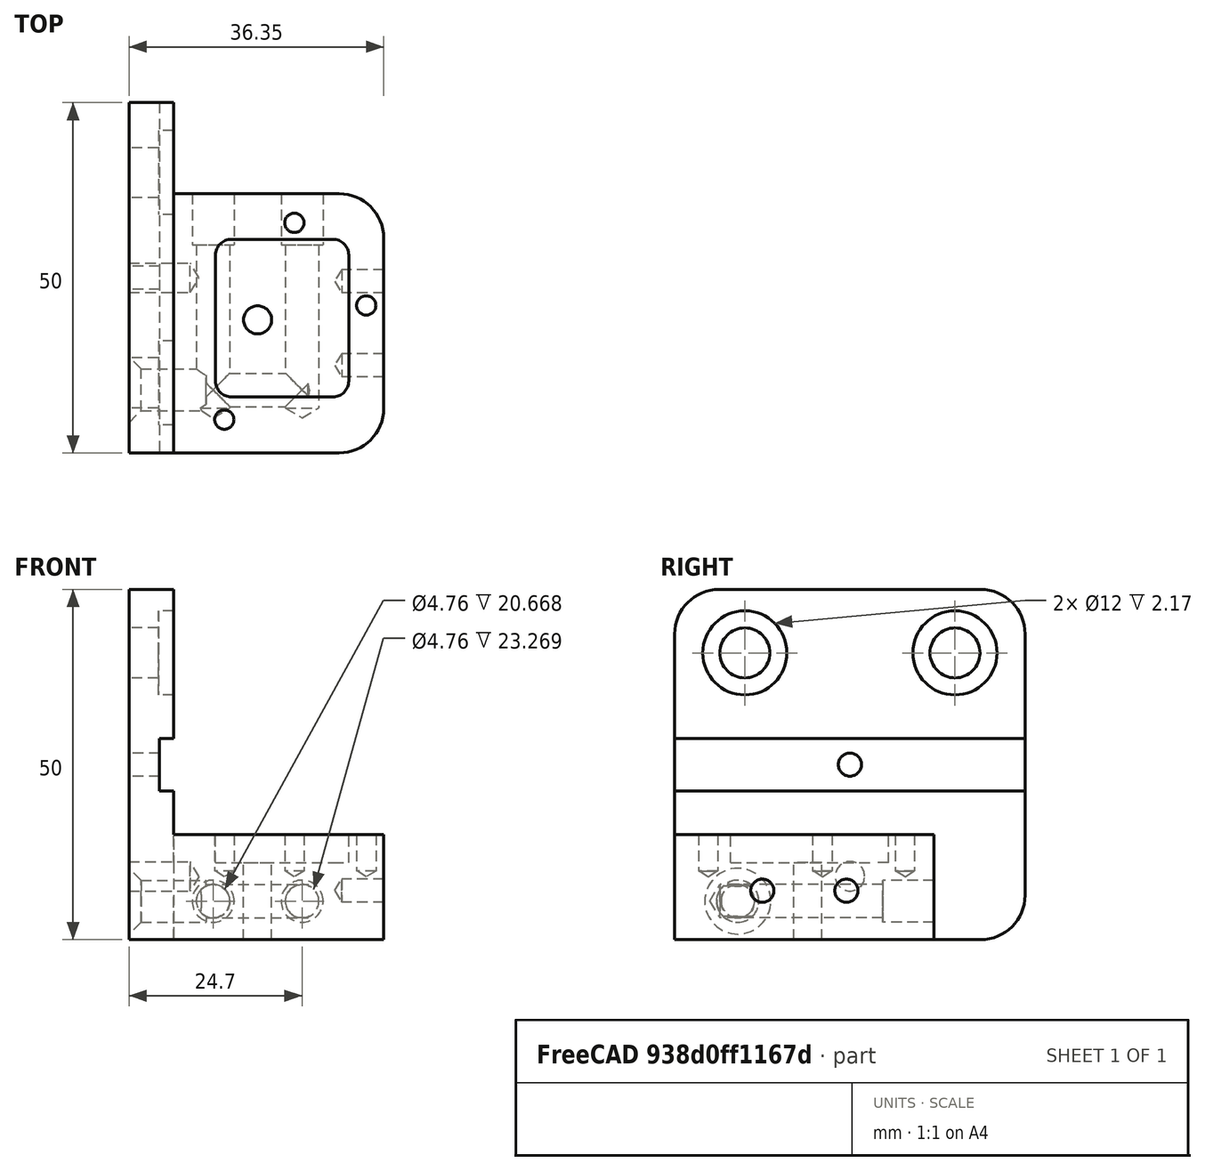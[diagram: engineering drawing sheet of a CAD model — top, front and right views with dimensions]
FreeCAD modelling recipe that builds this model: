
FCSTD DOCUMENT  (FreeCAD 0.19R24267 (Git))
Label: watercooled_block
License: All rights reserved
LicenseURL: http://en.wikipedia.org/wiki/All_rights_reserved
objects: TechDraw::DrawViewDimension×38, Sketcher::SketchObject×11, PartDesign::CoordinateSystem×10, TechDraw::DrawViewAnnotation×9, TechDraw::DrawLeaderLine×9, PartDesign::Hole×8, TechDraw::DrawProjGroupItem×6, PartDesign::Pad×2, PartDesign::Pocket×1, PartDesign::Fillet×1, PartDesign::Chamfer×1, PartDesign::Body×1, TechDraw::DrawSVGTemplate×1, TechDraw::DrawViewPart×1, TechDraw::DrawProjGroup×1, TechDraw::DrawPage×1, App::Part×1
note: 48 computed .brp shape members not serialized (recipe doc carries the construction recipe); baked Part::Feature solids carry a one-line shape summary decoded from their .brp

FEATURE [Sketcher::SketchObject] Sketch051
  FullyConstrained = false
  MapMode = 5
  Placement = pos=(0,0,0) rot=(1,0,0;1.5708rad)
  Support = -> [XZ_Plane061]
  sketch-geometry (10):
    g0: LineSegment StartX=18 StartY=0 StartZ=0 EndX=18 EndY=11 EndZ=0
    g1: LineSegment StartX=18 StartY=11 StartZ=0 EndX=-12 EndY=11 EndZ=0
    g2: LineSegment StartX=-18.35 StartY=0 StartZ=0 EndX=-18.35 EndY=50 EndZ=0
    g3: LineSegment StartX=-18.35 StartY=50 StartZ=0 EndX=-12 EndY=50 EndZ=0
    g4: LineSegment StartX=-12 StartY=50 StartZ=0 EndX=-12 EndY=28.75 EndZ=0
    g5: LineSegment StartX=-18.35 StartY=0 StartZ=0 EndX=18 EndY=0 EndZ=0
    g6: LineSegment StartX=-12 StartY=28.75 StartZ=0 EndX=-14 EndY=28.75 EndZ=0
    g7: LineSegment StartX=-14 StartY=28.75 StartZ=0 EndX=-14 EndY=21.25 EndZ=0
    g8: LineSegment StartX=-14 StartY=21.25 StartZ=0 EndX=-12 EndY=21.25 EndZ=0
    g9: LineSegment StartX=-12 StartY=21.25 StartZ=0 EndX=-12 EndY=11 EndZ=0
  constraints (29):
    c: Coincident(g0,g1)
    c: Horizontal(g1)
    c: Vertical(g0)
    c: Coincident(g2,g3)
    c: Coincident(g3,g4)
    c: Horizontal(g3)
    c: Vertical(g2)
    c: Vertical(g4)
    c: DistanceX(g3,g3) = 6.35
    c: DistanceX(g1,g-1) = 12
    c: Coincident(g1,g9)
    c: DistanceY(g0,g0) = 11
    c: DistanceY(g2,g2) = 50
    c: DistanceX(g-1,g0) = 18
    c: Coincident(g5,g2)
    c: Coincident(g5,g0)
    c: Horizontal(g5)
    c: PointOnObject(g-1,g5)
    c: Horizontal(g6)
    c: Coincident(g7,g6)
    c: Vertical(g7)
    c: Coincident(g8,g7)
    c: Horizontal(g8)
    c: Coincident(g4,g6)
    c: Coincident(g9,g8)
    c: Tangent(g4,g9)
    c: DistanceY(g7,g7) = 7.5
    c: DistanceY(g-1,g8) = 21.25
    c: DistanceX(g6,g6) = 2
FEATURE [PartDesign::Pad] Pad021  label="Pad022"
  AllowMultiFace = false
  Direction = (1,1,1)
  Length = 50
  Length2 = 100
  Midplane = true
  Placement = pos=(0,0,0) rot=(1,0,0;1.5708rad)
  Profile = -> Sketch051
  Type = 0
FEATURE [Sketcher::SketchObject] Sketch052
  AttachmentOffset = pos=(0,0,12) rot=(0,0,1;0rad)
  FullyConstrained = false
  MapMode = 5
  Placement = pos=(0,12,2.7e-15) rot=(0,0.707107,0.707107;3.14159rad)
  Support = -> [XZ_Plane061]
  sketch-geometry (3):
    g0: Circle CenterX=-6.35 CenterY=5.5 CenterZ=0 NormalX=0 NormalY=0 NormalZ=1 AngleXU=0 Radius=3.175
    g1: Circle CenterX=6.35 CenterY=5.5 CenterZ=0 NormalX=0 NormalY=0 NormalZ=1 AngleXU=0 Radius=3.175
    g2: LineSegment StartX=-6.35 StartY=5.5 StartZ=0 EndX=6.35 EndY=5.5 EndZ=0
  constraints (8):
    c: Diameter(g0) = 6.35
    c: Diameter(g1) = 6.35
    c: DistanceY(g-1,g0) = 5.5
    c: Coincident(g2,g0)
    c: Coincident(g2,g1)
    c: Horizontal(g2)
    c: DistanceX(g2,g2) = 12.7
    c: DistanceX(g0,g-1) = 6.35
FEATURE [Sketcher::SketchObject] Sketch053
  AttachmentOffset = pos=(0,0,18.35) rot=(0,0,1;0rad)
  FullyConstrained = false
  MapMode = 5
  Placement = pos=(-18.35,4.1e-15,-4.1e-15) rot=(-0.57735,0.57735,0.57735;4.18879rad)
  Support = -> [YZ_Plane061]
  sketch-geometry (1):
    g0: Circle CenterX=16 CenterY=5.5 CenterZ=0 NormalX=0 NormalY=0 NormalZ=1 AngleXU=0 Radius=2.5
  constraints (3):
    c: Diameter(g0) = 5
    c: DistanceY(g-1,g0) = 5.5
    c: DistanceX(g-1,g0) = 16
FEATURE [PartDesign::Hole] Hole006
  AllowMultiFace = false
  BaseFeature = -> Pad021
  Depth = 27
  DepthType = 0
  Diameter = 4.763
  DrillForDepth = false
  DrillPoint = 1
  DrillPointAngle = 118
  HoleCutCountersinkAngle = 90
  HoleCutCustomValues = false
  HoleCutDepth = 11
  HoleCutDiameter = 6
  HoleCutType = 1
  ModelActualThread = false
  Placement = pos=(0,0,0) rot=(1,0,0;1.5708rad)
  Profile = -> Sketch053
  Tapered = false
  TaperedAngle = 90
  ThreadAngle = 0
  ThreadClass = 0
  ThreadCutOffInner = 0
  ThreadCutOffOuter = 0
  ThreadDirection = 0
  ThreadFit = 0
  ThreadPitch = 0
  ThreadSize = 0
  ThreadType = 0
  Threaded = false
FEATURE [Sketcher::SketchObject] Sketch054
  FullyConstrained = false
  MapMode = 5
  Placement = pos=(0,0,0) rot=(0,1,0;3.14159rad)
  Support = -> [XY_Plane061]
  sketch-geometry (1):
    g0: Circle CenterX=0 CenterY=-6 CenterZ=0 NormalX=0 NormalY=0 NormalZ=1 AngleXU=0 Radius=2
  constraints (3):
    c: Diameter(g0) = 4
    c: PointOnObject(g0,g-2)
    c: DistanceY(g0,g-1) = 6
FEATURE [PartDesign::Hole] Hole007
  AllowMultiFace = false
  BaseFeature = -> Hole006
  Depth = 25
  DepthType = 1
  Diameter = 4
  DrillForDepth = false
  DrillPoint = 1
  DrillPointAngle = 118
  HoleCutCountersinkAngle = 90
  HoleCutCustomValues = false
  HoleCutDepth = 0
  HoleCutDiameter = 0
  HoleCutType = 0
  ModelActualThread = false
  Placement = pos=(0,0,0) rot=(1,0,0;1.5708rad)
  Profile = -> Sketch054
  Tapered = false
  TaperedAngle = 90
  ThreadAngle = 0
  ThreadClass = 0
  ThreadCutOffInner = 0
  ThreadCutOffOuter = 0
  ThreadDirection = 0
  ThreadFit = 0
  ThreadPitch = 0
  ThreadSize = 0
  ThreadType = 0
  Threaded = false
FEATURE [Sketcher::SketchObject] Sketch055
  AttachmentOffset = pos=(0,0,-12) rot=(0,0,1;0rad)
  FullyConstrained = false
  MapMode = 5
  Placement = pos=(-12,2.7e-15,-2.7e-15) rot=(0.57735,0.57735,0.57735;2.0944rad)
  Support = -> [YZ_Plane061]
  expr: Constraints[3] = 25 + 31.9 / 2
  sketch-geometry (2):
    g0: Circle CenterX=-15 CenterY=40.95 CenterZ=0 NormalX=0 NormalY=0 NormalZ=1 AngleXU=0 Radius=2.55
    g1: Circle CenterX=15 CenterY=40.95 CenterZ=0 NormalX=0 NormalY=0 NormalZ=1 AngleXU=0 Radius=2.55
  constraints (5):
    c: Diameter(g1) = 5.1
    c: Equal(g1,g0)
    c: DistanceX(g0,g1) = 30
    c: DistanceY(g-1,g0) = 40.95
    c: Symmetric(g0,g1,g-2)
FEATURE [PartDesign::Hole] Hole008
  AllowMultiFace = false
  BaseFeature = -> Hole007
  Depth = 25
  DepthType = 1
  Diameter = 7.14
  DrillForDepth = false
  DrillPoint = 1
  DrillPointAngle = 118
  HoleCutCountersinkAngle = 90
  HoleCutCustomValues = false
  HoleCutDepth = 2.17
  HoleCutDiameter = 12
  HoleCutType = 1
  ModelActualThread = false
  Placement = pos=(0,0,0) rot=(1,0,0;1.5708rad)
  Profile = -> Sketch055
  Tapered = false
  TaperedAngle = 90
  ThreadAngle = 0
  ThreadClass = 0
  ThreadCutOffInner = 0
  ThreadCutOffOuter = 0
  ThreadDirection = 0
  ThreadFit = 0
  ThreadPitch = 0
  ThreadSize = 0
  ThreadType = 0
  Threaded = false
  expr: HoleCutDepth = 6.35 - 4.18
FEATURE [Sketcher::SketchObject] Sketch056
  AttachmentOffset = pos=(0,0,18.35) rot=(0,0,1;0rad)
  FullyConstrained = false
  MapMode = 5
  Placement = pos=(-18.35,4.1e-15,-4.1e-15) rot=(-0.57735,0.57735,0.57735;4.18879rad)
  Support = -> [YZ_Plane061]
  expr: Constraints[2] = 25 - 31.9 / 2
  sketch-geometry (1):
    g0: Circle CenterX=0 CenterY=9.05 CenterZ=0 NormalX=0 NormalY=0 NormalZ=1 AngleXU=0 Radius=2.5
  constraints (3):
    c: PointOnObject(g0,g-2)
    c: Diameter(g0) = 5
    c: DistanceY(g-1,g0) = 9.05
FEATURE [Sketcher::SketchObject] Sketch057
  AttachmentOffset = pos=(0,0,11) rot=(0,0,1;0rad)
  FullyConstrained = false
  MapMode = 5
  Placement = pos=(0,0,11) rot=(0,0,1;0rad)
  Support = -> [XY_Plane061]
  sketch-geometry (4):
    g0: LineSegment StartX=23 StartY=32 StartZ=0 EndX=-12 EndY=32 EndZ=0
    g1: LineSegment StartX=-12 StartY=32 StartZ=0 EndX=-12 EndY=12 EndZ=0
    g2: LineSegment StartX=-12 StartY=12 StartZ=0 EndX=23 EndY=12 EndZ=0
    g3: LineSegment StartX=23 StartY=12 StartZ=0 EndX=23 EndY=32 EndZ=0
  constraints (12):
    c: Coincident(g0,g1)
    c: Coincident(g1,g2)
    c: Coincident(g2,g3)
    c: Coincident(g3,g0)
    c: Horizontal(g0)
    c: Horizontal(g2)
    c: Vertical(g1)
    c: Vertical(g3)
    c: DistanceX(g1,g-1) = 12
    c: DistanceX(g2,g2) = 35
    c: DistanceY(g3,g3) = 20
    c: DistanceY(g-1,g2) = 12
FEATURE [PartDesign::Pocket] Pocket019
  AllowMultiFace = false
  BaseFeature = -> Hole008
  Length = 5
  Length2 = 100
  Placement = pos=(0,0,0) rot=(1,0,0;1.5708rad)
  Profile = -> Sketch057
  Type = 1
FEATURE [PartDesign::Hole] Hole009
  AllowMultiFace = false
  BaseFeature = -> Pocket019
  Depth = 32
  DepthType = 0
  Diameter = 4.7625
  DrillForDepth = false
  DrillPoint = 1
  DrillPointAngle = 118
  HoleCutCountersinkAngle = 90
  HoleCutCustomValues = false
  HoleCutDepth = 7.3
  HoleCutDiameter = 6
  HoleCutType = 1
  ModelActualThread = false
  Placement = pos=(0,0,0) rot=(1,0,0;1.5708rad)
  Profile = -> Sketch052
  Tapered = false
  TaperedAngle = 90
  ThreadAngle = 0
  ThreadClass = 0
  ThreadCutOffInner = 0
  ThreadCutOffOuter = 0
  ThreadDirection = 0
  ThreadFit = 0
  ThreadPitch = 0
  ThreadSize = 0
  ThreadType = 0
  Threaded = false
  expr: Diameter = 3 / 16 * 25.4
FEATURE [Sketcher::SketchObject] Sketch058
  AttachmentOffset = pos=(0,0,11) rot=(0,0,1;0rad)
  FullyConstrained = false
  MapMode = 5
  Placement = pos=(0,0,11) rot=(0,0,1;0rad)
  Support = -> [XY_Plane061]
  sketch-geometry (12):
    g0: LineSegment StartX=13 StartY=-14.75 StartZ=0 EndX=13 EndY=3.25 EndZ=0
    g1: LineSegment StartX=10.75 StartY=5.5 StartZ=0 EndX=-3.75 EndY=5.5 EndZ=0
    g2: LineSegment StartX=-6 StartY=3.25 StartZ=0 EndX=-6 EndY=-14.75 EndZ=0
    g3: LineSegment StartX=-3.75 StartY=-17 StartZ=0 EndX=10.75 EndY=-17 EndZ=0
    g4: LineSegment StartX=18 StartY=-25 StartZ=0 EndX=-12 EndY=-25 EndZ=0
    g5: LineSegment StartX=-12 StartY=-25 StartZ=0 EndX=-12 EndY=12 EndZ=0
    g6: LineSegment StartX=-12 StartY=12 StartZ=0 EndX=18 EndY=12 EndZ=0
    g7: LineSegment StartX=18 StartY=12 StartZ=0 EndX=18 EndY=-25 EndZ=0
    g8: ArcOfCircle CenterX=10.75 CenterY=3.25 CenterZ=0 NormalX=0 NormalY=0 NormalZ=1 AngleXU=0 Radius=2.25 StartAngle=3.758e-13 EndAngle=1.5708
    g9: ArcOfCircle CenterX=-3.75 CenterY=3.25 CenterZ=0 NormalX=0 NormalY=0 NormalZ=1 AngleXU=0 Radius=2.25 StartAngle=1.5708 EndAngle=3.14159
    g10: ArcOfCircle CenterX=-3.75 CenterY=-14.75 CenterZ=0 NormalX=0 NormalY=0 NormalZ=1 AngleXU=0 Radius=2.25 StartAngle=3.14159 EndAngle=4.71239
    g11: ArcOfCircle CenterX=10.75 CenterY=-14.75 CenterZ=0 NormalX=0 NormalY=0 NormalZ=1 AngleXU=0 Radius=2.25 StartAngle=4.71239 EndAngle=6.28319
  constraints (32):
    c: Vertical(g0)
    c: Horizontal(g1)
    c: Vertical(g2)
    c: Horizontal(g3)
    c: Horizontal(g4)
    c: Coincident(g4,g5)
    c: Vertical(g5)
    c: Coincident(g5,g6)
    c: Horizontal(g6)
    c: Coincident(g6,g7)
    c: Vertical(g7)
    c: Tangent(g1,g8) = -1.5708
    c: Tangent(g0,g8) = -1.5708
    c: Tangent(g1,g9) = -1.5708
    c: Tangent(g2,g9) = -1.5708
    c: Tangent(g3,g10) = -1.5708
    c: Tangent(g2,g10) = -1.5708
    c: DistanceY(g-1,g6) = 12
    c: DistanceY(g4,g-1) = 25
    c: DistanceY(g-1,g1) = 5.5
    c: DistanceX(g2,g-1) = 6
    c: DistanceX(g-1,g0) = 13
    c: DistanceX(g-1,g6) = 18
    c: Equal(g9,g8)
    c: Diameter(g10) = 4.5
    c: DistanceX(g5,g-1) = 12
    c: Coincident(g7,g4)
    c: Tangent(g0,g11) = -1.5708
    c: Tangent(g3,g11) = -1.5708
    c: Equal(g10,g11)
    c: DistanceY(g3,g-1) = 17
    c: Equal(g10,g9)
FEATURE [PartDesign::Pad] Pad022  label="Pad023"
  AllowMultiFace = false
  BaseFeature = -> Hole009
  Direction = (1,1,1)
  Length = 4
  Length2 = 100
  Placement = pos=(0,0,0) rot=(1,0,0;1.5708rad)
  Profile = -> Sketch058
  Type = 0
FEATURE [Sketcher::SketchObject] Sketch059
  AttachmentOffset = pos=(0,0,15) rot=(0,0,1;0rad)
  FullyConstrained = false
  MapMode = 5
  Placement = pos=(0,0,15) rot=(0,0,1;0rad)
  Support = -> [XY_Plane061]
  sketch-geometry (3):
    g0: Circle CenterX=15.5 CenterY=-3.95 CenterZ=0 NormalX=0 NormalY=0 NormalZ=1 AngleXU=0 Radius=1.5
    g1: Circle CenterX=5.25 CenterY=7.85 CenterZ=0 NormalX=0 NormalY=0 NormalZ=1 AngleXU=0 Radius=1.5
    g2: Circle CenterX=-4.75 CenterY=-20.25 CenterZ=0 NormalX=0 NormalY=0 NormalZ=1 AngleXU=0 Radius=1.5
  constraints (9):
    c: DistanceY(g2,g-1) = 20.25
    c: DistanceX(g2,g-1) = 4.75
    c: DistanceX(g-1,g0) = 15.5
    c: DistanceX(g-1,g1) = 5.25
    c: DistanceY(g-1,g1) = 7.85
    c: DistanceY(g0,g-1) = 3.95
    c: Equal(g1,g0)
    c: Equal(g0,g2)
    c: Diameter(g1) = 3
FEATURE [PartDesign::Hole] Hole010
  AllowMultiFace = false
  BaseFeature = -> Pad022
  Depth = 6
  DepthType = 0
  Diameter = 1.4
  DrillForDepth = false
  DrillPoint = 1
  DrillPointAngle = 118
  HoleCutCountersinkAngle = 90
  HoleCutCustomValues = false
  HoleCutDepth = 0
  HoleCutDiameter = 2.5
  HoleCutType = 0
  ModelActualThread = false
  Placement = pos=(0,0,0) rot=(1,0,0;1.5708rad)
  Profile = -> Sketch059
  Tapered = false
  TaperedAngle = 90
  ThreadAngle = 0
  ThreadClass = 0
  ThreadCutOffInner = 0
  ThreadCutOffOuter = 0
  ThreadDirection = 0
  ThreadFit = 0
  ThreadPitch = 0
  ThreadSize = 2
  ThreadType = 1
  Threaded = false
FEATURE [PartDesign::Hole] Hole011
  AllowMultiFace = false
  BaseFeature = -> Hole010
  Depth = 10
  DepthType = 0
  Diameter = 1.6
  DrillForDepth = false
  DrillPoint = 1
  DrillPointAngle = 118
  HoleCutCountersinkAngle = 90
  HoleCutCustomValues = false
  HoleCutDepth = 0
  HoleCutDiameter = 5
  HoleCutType = 0
  ModelActualThread = false
  Placement = pos=(0,0,0) rot=(1,0,0;1.5708rad)
  Profile = -> Sketch056
  Tapered = false
  TaperedAngle = 90
  ThreadAngle = 60
  ThreadClass = 0
  ThreadCutOffInner = 0.0433013
  ThreadCutOffOuter = 0.0866025
  ThreadDirection = 1
  ThreadFit = 0
  ThreadPitch = 0.4
  ThreadSize = 6
  ThreadType = 1
  Threaded = true
FEATURE [Sketcher::SketchObject] Sketch060
  FullyConstrained = false
  MapMode = 5
  Placement = pos=(0,0,0) rot=(0.57735,0.57735,0.57735;2.0944rad)
  Support = -> [YZ_Plane061]
  sketch-geometry (1):
    g0: Circle CenterX=0 CenterY=25 CenterZ=0 NormalX=0 NormalY=0 NormalZ=1 AngleXU=0 Radius=1.5
  constraints (3):
    c: PointOnObject(g0,g-2)
    c: DistanceY(g-1,g0) = 25
    c: Diameter(g0) = 3
FEATURE [PartDesign::Hole] Hole012
  AllowMultiFace = false
  BaseFeature = -> Hole011
  Depth = 25
  DepthType = 1
  Diameter = 1.6
  DrillForDepth = false
  DrillPoint = 1
  DrillPointAngle = 118
  HoleCutCountersinkAngle = 90
  HoleCutCustomValues = false
  HoleCutDepth = 0
  HoleCutDiameter = 3
  HoleCutType = 0
  ModelActualThread = false
  Placement = pos=(0,0,0) rot=(1,0,0;1.5708rad)
  Profile = -> Sketch060
  Tapered = false
  TaperedAngle = 90
  ThreadAngle = 0
  ThreadClass = 0
  ThreadCutOffInner = 0
  ThreadCutOffOuter = 0
  ThreadDirection = 0
  ThreadFit = 0
  ThreadPitch = 0
  ThreadSize = 3
  ThreadType = 1
  Threaded = false
FEATURE [PartDesign::Fillet] Fillet004
  Base = -> Hole012 [Edge9,Edge31,Edge57,Edge23,Edge19,Edge51,Edge1]
  BaseFeature = -> Hole012
  Placement = pos=(0,0,0) rot=(1,0,0;1.5708rad)
  Radius = 6.35
  SupportTransform = true
FEATURE [PartDesign::Chamfer] Chamfer002
  Angle = 45
  Base = -> Fillet004 [Edge25]
  BaseFeature = -> Fillet004
  ChamferType = 0
  FlipDirection = false
  Placement = pos=(0,0,0) rot=(1,0,0;1.5708rad)
  Size = 1.7
  Size2 = 1
  SupportTransform = true
FEATURE [Sketcher::SketchObject] Sketch073
  AttachmentOffset = pos=(0,0,18) rot=(0,0,1;0rad)
  FullyConstrained = false
  MapMode = 5
  Placement = pos=(18,-4e-15,4e-15) rot=(0.57735,0.57735,0.57735;2.0944rad)
  Support = -> [YZ_Plane061]
  sketch-geometry (2):
    g0: Circle CenterX=-0.5 CenterY=7 CenterZ=0 NormalX=0 NormalY=0 NormalZ=1 AngleXU=0 Radius=1.5
    g1: Circle CenterX=-12.5 CenterY=7 CenterZ=0 NormalX=0 NormalY=0 NormalZ=1 AngleXU=0 Radius=1.5
  constraints (6):
    c: Horizontal(g1,g0)
    c: Equal(g1,g0)
    c: Diameter(g0) = 3
    c: DistanceY(g-1,g0) = 7
    c: DistanceX(g1,g0) = 12
    c: DistanceX(g0,g-1) = 0.5
FEATURE [PartDesign::Hole] Hole014
  BaseFeature = -> Chamfer002
  Depth = 7
  DepthType = 0
  Diameter = 1.6
  DrillForDepth = false
  DrillPoint = 1
  DrillPointAngle = 118
  HoleCutCountersinkAngle = 90
  HoleCutCustomValues = false
  HoleCutDepth = 0
  HoleCutDiameter = 3
  HoleCutType = 0
  ModelActualThread = false
  Placement = pos=(0,0,0) rot=(1,0,0;1.5708rad)
  Profile = -> Sketch073
  Tapered = false
  TaperedAngle = 90
  ThreadAngle = 0
  ThreadClass = 0
  ThreadCutOffInner = 0
  ThreadCutOffOuter = 0
  ThreadDirection = 0
  ThreadFit = 0
  ThreadPitch = 0
  ThreadSize = 3
  ThreadType = 1
  Threaded = false
FEATURE [PartDesign::Body] Body021  label="block"
  Group = -> [Sketch051,Pad021,Sketch052,Sketch053,Hole006,Sketch054,Hole007,Sketch055,Hole008,Sketch056,Sketch057,Pocket019,Hole009,Sketch058,Pad022,Sketch059,Hole010,Hole011,Sketch060,Hole012,Fillet004,Chamfer002,Sketch073,Hole014]
  Origin = -> Origin061
  Tip = -> Hole014
FEATURE [TechDraw::DrawSVGTemplate] Template002
  EditableTexts = Author=Alex Neufeld; DWG_num=2020-105; Date=09/05/2020; Revision=1; Scale=NTS; Subtitle=For 20mm V-Slot Rail; Title=Watercooled Print Head
  Height = 215.9
  Orientation = 1
  Width = 279.4
FEATURE [TechDraw::DrawViewPart] View002
  CoarseView = false
  Direction = (0.577,-0.577,0.577)
  Focus = 100
  HardHidden = false
  IsoCount = 0
  IsoHidden = false
  IsoVisible = false
  LockPosition = false
  Perspective = false
  Rotation = 0
  Scale = 0.5
  ScaleType = 0
  SeamHidden = false
  SeamVisible = true
  SmoothHidden = false
  SmoothVisible = true
  X = 30.583
  XDirection = (0.707,0.707,0)
  Y = 183.107
FEATURE [TechDraw::DrawProjGroupItem] ProjItem007  label="Front002"
  CoarseView = false
  Direction = (1,-1e-16,0)
  Focus = 100
  HardHidden = false
  IsoCount = 0
  IsoHidden = false
  IsoVisible = false
  LockPosition = true
  Perspective = false
  Rotation = 0
  RotationVector = (1,0,0)
  ScaleType = 2
  SeamHidden = false
  SeamVisible = true
  SmoothHidden = false
  SmoothVisible = true
  Source = -> [Body021]
  Type = 0
  X = 0
  XDirection = (1e-16,1,0)
  Y = 0
FEATURE [TechDraw::DrawProjGroupItem] ProjItem008  label="Left001"
  CoarseView = false
  Direction = (0,-1,0)
  Focus = 100
  HardHidden = false
  IsoCount = 0
  IsoHidden = false
  IsoVisible = false
  LockPosition = true
  Perspective = false
  Rotation = 0
  RotationVector = (1,0,0)
  ScaleType = 2
  SeamHidden = false
  SeamVisible = true
  SmoothHidden = false
  SmoothVisible = true
  Source = -> [Body021]
  Type = 1
  X = 65
  XDirection = (1,0,0)
  Y = 0
FEATURE [TechDraw::DrawProjGroupItem] ProjItem009  label="Rear"
  CoarseView = false
  Direction = (-1,1e-16,0)
  Focus = 100
  HardHidden = false
  IsoCount = 0
  IsoHidden = false
  IsoVisible = false
  LockPosition = true
  Perspective = false
  Rotation = 0
  RotationVector = (1,0,0)
  ScaleType = 2
  SeamHidden = false
  SeamVisible = true
  SmoothHidden = false
  SmoothVisible = true
  Source = -> [Body021]
  Type = 3
  X = 130
  XDirection = (-1e-16,-1,0)
  Y = 0
FEATURE [TechDraw::DrawProjGroupItem] ProjItem010  label="Right001"
  CoarseView = false
  Direction = (2e-16,1,0)
  Focus = 100
  HardHidden = false
  IsoCount = 0
  IsoHidden = false
  IsoVisible = false
  LockPosition = true
  Perspective = false
  Rotation = 0
  RotationVector = (1,0,0)
  ScaleType = 2
  SeamHidden = false
  SeamVisible = true
  SmoothHidden = false
  SmoothVisible = true
  Source = -> [Body021]
  Type = 2
  X = -65
  XDirection = (-1,2e-16,0)
  Y = 0
FEATURE [TechDraw::DrawProjGroupItem] ProjItem012  label="Top"
  CoarseView = false
  Direction = (0,0,1)
  Focus = 100
  HardHidden = false
  IsoCount = 0
  IsoHidden = false
  IsoVisible = false
  LockPosition = true
  Perspective = false
  Rotation = 0
  RotationVector = (1,0,0)
  ScaleType = 2
  SeamHidden = false
  SeamVisible = true
  SmoothHidden = false
  SmoothVisible = true
  Source = -> [Body021]
  Type = 4
  X = 0
  XDirection = (1e-16,1,0)
  Y = -70.3637
FEATURE [TechDraw::DrawProjGroupItem] ProjItem013  label="Bottom002"
  CoarseView = false
  Direction = (0,0,-1)
  Focus = 100
  HardHidden = false
  IsoCount = 0
  IsoHidden = false
  IsoVisible = false
  LockPosition = false
  Perspective = false
  Rotation = 0
  RotationVector = (1,0,0)
  ScaleType = 2
  SeamHidden = false
  SeamVisible = true
  SmoothHidden = false
  SmoothVisible = true
  Source = -> [Body021]
  Type = 5
  X = 0
  XDirection = (1e-16,1,0)
  Y = 15
FEATURE [TechDraw::DrawProjGroup] ProjGroup002
  Anchor = -> ProjItem007
  AutoDistribute = true
  LockPosition = false
  ProjectionType = 0
  Rotation = 0
  ScaleType = 0
  Source = -> [Body021]
  Views = -> [ProjItem007,ProjItem008,ProjItem009,ProjItem010,ProjItem012,ProjItem013]
  X = 103.639
  Y = 118.803
  spacingX = 15
  spacingY = 15
FEATURE [TechDraw::DrawViewDimension] Dimension024
  Arbitrary = false
  ArbitraryTolerances = false
  EqualTolerance = false
  FormatSpec = R%.2f
  FormatSpecOverTolerance = %+.2f
  FormatSpecUnderTolerance = %+.2f
  Inverted = false
  LockPosition = false
  MeasureType = 1
  OverTolerance = 0
  References2D = -> [ProjItem013]
  Rotation = 0
  ScaleType = 0
  TheoreticalExact = false
  Type = 4
  UnderTolerance = 0
  X = 19.1509
  Y = 14.0701
FEATURE [TechDraw::DrawViewDimension] Dimension025
  Arbitrary = false
  ArbitraryTolerances = false
  EqualTolerance = false
  FormatSpec = %.2f
  FormatSpecOverTolerance = %+.2f
  FormatSpecUnderTolerance = %+.2f
  Inverted = false
  LockPosition = false
  MeasureType = 1
  OverTolerance = 0
  References2D = -> [ProjItem013]
  Rotation = 0
  ScaleType = 0
  TheoreticalExact = false
  Type = 2
  UnderTolerance = 0
  X = -34.234
  Y = -0.195417
FEATURE [TechDraw::DrawViewDimension] Dimension026
  Arbitrary = false
  ArbitraryTolerances = false
  EqualTolerance = false
  FormatSpec = %.2f
  FormatSpecOverTolerance = %+.2f
  FormatSpecUnderTolerance = %+.2f
  Inverted = false
  LockPosition = false
  MeasureType = 1
  OverTolerance = 0
  References2D = -> [ProjItem013]
  Rotation = 0
  ScaleType = 0
  TheoreticalExact = false
  Type = 1
  UnderTolerance = 0
  X = -0.586252
  Y = -21.9856
FEATURE [TechDraw::DrawViewDimension] Dimension028
  Arbitrary = false
  ArbitraryTolerances = false
  EqualTolerance = false
  FormatSpec = %.2f
  FormatSpecOverTolerance = %+.2f
  FormatSpecUnderTolerance = %+.2f
  Inverted = false
  LockPosition = false
  MeasureType = 1
  OverTolerance = 0
  References2D = -> [ProjItem013]
  Rotation = 0
  ScaleType = 0
  TheoreticalExact = false
  Type = 1
  UnderTolerance = 0
  X = -16.2817
  Y = 7.29445
FEATURE [TechDraw::DrawViewDimension] Dimension029
  Arbitrary = false
  ArbitraryTolerances = false
  EqualTolerance = false
  FormatSpec = %.2f
  FormatSpecOverTolerance = %+.2f
  FormatSpecUnderTolerance = %+.2f
  Inverted = false
  LockPosition = false
  MeasureType = 1
  OverTolerance = 0
  References2D = -> [ProjItem013]
  Rotation = 0
  ScaleType = 0
  TheoreticalExact = false
  Type = 2
  UnderTolerance = 0
  X = 28.5566
  Y = -6.20621
FEATURE [TechDraw::DrawViewDimension] Dimension030
  Arbitrary = false
  ArbitraryTolerances = false
  EqualTolerance = false
  FormatSpec = %.2f
  FormatSpecOverTolerance = %+.2f
  FormatSpecUnderTolerance = %+.2f
  Inverted = false
  LockPosition = false
  MeasureType = 1
  OverTolerance = 0
  References2D = -> [ProjItem013]
  Rotation = 0
  ScaleType = 0
  TheoreticalExact = false
  Type = 1
  UnderTolerance = 0
  X = 37.3578
  Y = 3.61298
FEATURE [TechDraw::DrawViewDimension] Dimension031
  Arbitrary = false
  ArbitraryTolerances = false
  EqualTolerance = false
  FormatSpec = %.2f
  FormatSpecOverTolerance = %+.2f
  FormatSpecUnderTolerance = %+.2f
  Inverted = false
  LockPosition = false
  MeasureType = 1
  OverTolerance = 0
  References2D = -> [ProjItem008]
  Rotation = 0
  ScaleType = 0
  TheoreticalExact = false
  Type = 1
  UnderTolerance = 0
  X = -5.76623
  Y = 0.287702
FEATURE [TechDraw::DrawViewDimension] Dimension032
  Arbitrary = false
  ArbitraryTolerances = false
  EqualTolerance = false
  FormatSpec = %.2f
  FormatSpecOverTolerance = %+.2f
  FormatSpecUnderTolerance = %+.2f
  Inverted = false
  LockPosition = false
  MeasureType = 1
  OverTolerance = 0
  References2D = -> [ProjItem008]
  Rotation = 0
  ScaleType = 0
  TheoreticalExact = false
  Type = 2
  UnderTolerance = 0
  X = -0.901396
  Y = 15.1348
FEATURE [TechDraw::DrawViewDimension] Dimension033
  Arbitrary = false
  ArbitraryTolerances = false
  EqualTolerance = false
  FormatSpec = %.2f
  FormatSpecOverTolerance = %+.2f
  FormatSpecUnderTolerance = %+.2f
  Inverted = false
  LockPosition = false
  MeasureType = 1
  OverTolerance = 0
  References2D = -> [ProjItem008]
  Rotation = 0
  ScaleType = 0
  TheoreticalExact = false
  Type = 2
  UnderTolerance = 0
  X = 21.8895
  Y = -17.5
FEATURE [TechDraw::DrawViewDimension] Dimension035
  Arbitrary = false
  ArbitraryTolerances = false
  EqualTolerance = false
  FormatSpec = %.2f
  FormatSpecOverTolerance = %+.2f
  FormatSpecUnderTolerance = %+.2f
  Inverted = false
  LockPosition = false
  MeasureType = 1
  OverTolerance = 0
  References2D = -> [ProjItem009]
  Rotation = 0
  ScaleType = 0
  TheoreticalExact = false
  Type = 2
  UnderTolerance = 0
  X = 28.1125
  Y = -31.9901
FEATURE [TechDraw::DrawViewDimension] Dimension036
  Arbitrary = false
  ArbitraryTolerances = false
  EqualTolerance = false
  FormatSpec = %.2f
  FormatSpecOverTolerance = %+.2f
  FormatSpecUnderTolerance = %+.2f
  Inverted = false
  LockPosition = false
  MeasureType = 1
  OverTolerance = 0
  References2D = -> [ProjItem009]
  Rotation = 0
  ScaleType = 0
  TheoreticalExact = false
  Type = 1
  UnderTolerance = 0
  X = 12.1513
  Y = -8.7684
FEATURE [TechDraw::DrawViewDimension] Dimension037
  Arbitrary = false
  ArbitraryTolerances = false
  EqualTolerance = false
  FormatSpec = %.2f
  FormatSpecOverTolerance = %+.2f
  FormatSpecUnderTolerance = %+.2f
  Inverted = false
  LockPosition = false
  MeasureType = 1
  OverTolerance = 0
  References2D = -> [ProjItem009]
  Rotation = 0
  ScaleType = 0
  TheoreticalExact = false
  Type = 2
  UnderTolerance = 0
  X = 1.14094
  Y = -29.3403
FEATURE [TechDraw::DrawViewDimension] Dimension038
  Arbitrary = false
  ArbitraryTolerances = false
  EqualTolerance = false
  FormatSpec = %.2f
  FormatSpecOverTolerance = %+.2f
  FormatSpecUnderTolerance = %+.2f
  Inverted = false
  LockPosition = false
  MeasureType = 1
  OverTolerance = 0
  References2D = -> [ProjItem009]
  Rotation = 0
  ScaleType = 0
  TheoreticalExact = false
  Type = 2
  UnderTolerance = 0
  X = -34.6499
  Y = -0.866784
FEATURE [TechDraw::DrawViewDimension] Dimension039
  Arbitrary = false
  ArbitraryTolerances = false
  EqualTolerance = false
  FormatSpec = %.2f
  FormatSpecOverTolerance = %+.2f
  FormatSpecUnderTolerance = %+.2f
  Inverted = false
  LockPosition = false
  MeasureType = 1
  OverTolerance = 0
  References2D = -> [ProjItem009]
  Rotation = 0
  ScaleType = 0
  TheoreticalExact = false
  Type = 1
  UnderTolerance = 0
  X = 18.4523
  Y = 34.8435
FEATURE [TechDraw::DrawViewDimension] Dimension040
  Arbitrary = false
  ArbitraryTolerances = false
  EqualTolerance = false
  FormatSpec = %.2f
  FormatSpecOverTolerance = %+.2f
  FormatSpecUnderTolerance = %+.2f
  Inverted = false
  LockPosition = false
  MeasureType = 1
  OverTolerance = 0
  References2D = -> [ProjItem009]
  Rotation = 0
  ScaleType = 0
  TheoreticalExact = false
  Type = 1
  UnderTolerance = 0
  X = -5.41184
  Y = 32.4516
FEATURE [TechDraw::DrawViewDimension] Dimension042
  Arbitrary = false
  ArbitraryTolerances = false
  EqualTolerance = false
  FormatSpec = %.2f
  FormatSpecOverTolerance = %+.2f
  FormatSpecUnderTolerance = %+.2f
  Inverted = false
  LockPosition = false
  MeasureType = 1
  OverTolerance = 0
  References2D = -> [ProjItem012]
  Rotation = 0
  ScaleType = 0
  TheoreticalExact = false
  Type = 2
  UnderTolerance = 0
  X = -29.4955
  Y = 11.4157
FEATURE [TechDraw::DrawViewDimension] Dimension043
  Arbitrary = false
  ArbitraryTolerances = false
  EqualTolerance = false
  FormatSpec = %.2f
  FormatSpecOverTolerance = %+.2f
  FormatSpecUnderTolerance = %+.2f
  Inverted = false
  LockPosition = false
  MeasureType = 1
  OverTolerance = 0
  References2D = -> [ProjItem012]
  Rotation = 0
  ScaleType = 0
  TheoreticalExact = false
  Type = 2
  UnderTolerance = 0
  X = -36.1103
  Y = 7.53454
FEATURE [TechDraw::DrawViewDimension] Dimension044
  Arbitrary = false
  ArbitraryTolerances = false
  EqualTolerance = false
  FormatSpec = %.2f
  FormatSpecOverTolerance = %+.2f
  FormatSpecUnderTolerance = %+.2f
  Inverted = false
  LockPosition = false
  MeasureType = 1
  OverTolerance = 0
  References2D = -> [ProjItem012]
  Rotation = 0
  ScaleType = 0
  TheoreticalExact = false
  Type = 2
  UnderTolerance = 0
  X = -42.6347
  Y = 2.67713
FEATURE [TechDraw::DrawViewDimension] Dimension045
  Arbitrary = false
  ArbitraryTolerances = false
  EqualTolerance = false
  FormatSpec = %.2f
  FormatSpecOverTolerance = %+.2f
  FormatSpecUnderTolerance = %+.2f
  Inverted = false
  LockPosition = false
  MeasureType = 1
  OverTolerance = 0
  References2D = -> [ProjItem012]
  Rotation = 0
  ScaleType = 0
  TheoreticalExact = false
  Type = 1
  UnderTolerance = 0
  X = -14.7458
  Y = 24.3035
FEATURE [TechDraw::DrawViewDimension] Dimension046
  Arbitrary = false
  ArbitraryTolerances = false
  EqualTolerance = false
  FormatSpec = %.2f
  FormatSpecOverTolerance = %+.2f
  FormatSpecUnderTolerance = %+.2f
  Inverted = false
  LockPosition = false
  MeasureType = 1
  OverTolerance = 0
  References2D = -> [ProjItem012]
  Rotation = 0
  ScaleType = 0
  TheoreticalExact = false
  Type = 1
  UnderTolerance = 0
  X = -15.4599
  Y = -23.8107
FEATURE [TechDraw::DrawViewDimension] Dimension047
  Arbitrary = false
  ArbitraryTolerances = false
  EqualTolerance = false
  FormatSpec = %.2f
  FormatSpecOverTolerance = %+.2f
  FormatSpecUnderTolerance = %+.2f
  Inverted = false
  LockPosition = false
  MeasureType = 1
  OverTolerance = 0
  References2D = -> [ProjItem012]
  Rotation = 0
  ScaleType = 0
  TheoreticalExact = false
  Type = 1
  UnderTolerance = 0
  X = -8.2936
  Y = -30.4726
FEATURE [TechDraw::DrawViewDimension] Dimension048
  Arbitrary = false
  ArbitraryTolerances = false
  EqualTolerance = false
  FormatSpec = %.2f
  FormatSpecOverTolerance = %+.2f
  FormatSpecUnderTolerance = %+.2f
  Inverted = false
  LockPosition = false
  MeasureType = 1
  OverTolerance = 0
  References2D = -> [ProjItem007]
  Rotation = 0
  ScaleType = 0
  TheoreticalExact = false
  Type = 2
  UnderTolerance = 0
  X = -34.5365
  Y = -11.6191
FEATURE [TechDraw::DrawViewDimension] Dimension049
  Arbitrary = false
  ArbitraryTolerances = false
  EqualTolerance = false
  FormatSpec = %.2f
  FormatSpecOverTolerance = %+.2f
  FormatSpecUnderTolerance = %+.2f
  Inverted = false
  LockPosition = false
  MeasureType = 1
  OverTolerance = 0
  References2D = -> [ProjItem008]
  Rotation = 0
  ScaleType = 0
  TheoreticalExact = false
  Type = 2
  UnderTolerance = 0
  X = -24.7797
  Y = -13.3181
FEATURE [TechDraw::DrawViewDimension] Dimension050
  Arbitrary = false
  ArbitraryTolerances = false
  EqualTolerance = false
  FormatSpec = %.2f
  FormatSpecOverTolerance = %+.2f
  FormatSpecUnderTolerance = %+.2f
  Inverted = false
  LockPosition = false
  MeasureType = 1
  OverTolerance = 0
  References2D = -> [ProjItem007]
  Rotation = 0
  ScaleType = 0
  TheoreticalExact = false
  Type = 2
  UnderTolerance = 0
  X = -41.5171
  Y = -22.3563
FEATURE [TechDraw::DrawViewDimension] Dimension051
  Arbitrary = false
  ArbitraryTolerances = false
  EqualTolerance = false
  FormatSpec = %.2f
  FormatSpecOverTolerance = %+.2f
  FormatSpecUnderTolerance = %+.2f
  Inverted = false
  LockPosition = false
  MeasureType = 1
  OverTolerance = 0
  References2D = -> [ProjItem007]
  Rotation = 0
  ScaleType = 0
  TheoreticalExact = false
  Type = 1
  UnderTolerance = 0
  X = 6.60144
  Y = -35.5375
FEATURE [TechDraw::DrawViewDimension] Dimension052
  Arbitrary = false
  ArbitraryTolerances = false
  EqualTolerance = false
  FormatSpec = %.2f
  FormatSpecOverTolerance = %+.2f
  FormatSpecUnderTolerance = %+.2f
  Inverted = false
  LockPosition = false
  MeasureType = 1
  OverTolerance = 0
  References2D = -> [ProjItem007]
  Rotation = 0
  ScaleType = 0
  TheoreticalExact = false
  Type = 1
  UnderTolerance = 0
  X = 6.19512
  Y = -28.64
FEATURE [TechDraw::DrawViewAnnotation] Annotation
  Font = Sans Serif
  LineSpace = 80
  LockPosition = false
  MaxWidth = -1
  Rotation = 0
  ScaleType = 0
  Text = Drill 3/16" - Depth 27.0 mm | Drill 5mm - Depth 11.0 mm | Tap M6x1.0 | Countersink to match M6 plug
  TextSize = 2.5
  TextStyle = 0
  X = 243.063
  Y = 71.5534
FEATURE [TechDraw::DrawViewDimension] Dimension053
  Arbitrary = false
  ArbitraryTolerances = false
  EqualTolerance = false
  FormatSpec = %.2f
  FormatSpecOverTolerance = %+.2f
  FormatSpecUnderTolerance = %+.2f
  Inverted = false
  LockPosition = false
  MeasureType = 1
  OverTolerance = 0
  References2D = -> [ProjItem010]
  Rotation = 0
  ScaleType = 0
  TheoreticalExact = false
  Type = 2
  UnderTolerance = 0
  X = -25.1679
  Y = -21.1101
FEATURE [TechDraw::DrawViewDimension] Dimension054
  Arbitrary = false
  ArbitraryTolerances = false
  EqualTolerance = false
  FormatSpec = %.2f
  FormatSpecOverTolerance = %+.2f
  FormatSpecUnderTolerance = %+.2f
  Inverted = false
  LockPosition = false
  MeasureType = 1
  OverTolerance = 0
  References2D = -> [ProjItem010]
  Rotation = 0
  ScaleType = 0
  TheoreticalExact = false
  Type = 1
  UnderTolerance = 0
  X = 2.56697
  Y = -35.7193
FEATURE [TechDraw::DrawViewDimension] Dimension055
  Arbitrary = false
  ArbitraryTolerances = false
  EqualTolerance = false
  FormatSpec = %.2f
  FormatSpecOverTolerance = %+.2f
  FormatSpecUnderTolerance = %+.2f
  Inverted = false
  LockPosition = false
  MeasureType = 1
  OverTolerance = 0
  References2D = -> [ProjItem010]
  Rotation = 0
  ScaleType = 0
  TheoreticalExact = false
  Type = 1
  UnderTolerance = 0
  X = -15.1824
  Y = -41.0119
FEATURE [TechDraw::DrawViewAnnotation] Annotation001
  Font = Sans Serif
  LineSpace = 80
  LockPosition = false
  MaxWidth = -1
  Rotation = 0
  ScaleType = 0
  Text = Drill 3/16" - Depth 32.0mm | Drill 5.0mm - Depth 7.3mm | Tap M6x1.0
  TextSize = 2.5
  TextStyle = 0
  X = 31.0661
  Y = 115.642
FEATURE [TechDraw::DrawViewAnnotation] Annotation002
  Font = Sans Serif
  LineSpace = 80
  LockPosition = false
  MaxWidth = -1
  Rotation = 0
  ScaleType = 0
  Text = Through Drill 1/8" & tap M4x0.7
  TextSize = 2.5
  TextStyle = 0
  X = 153.114
  Y = 56.3806
FEATURE [TechDraw::DrawViewAnnotation] Annotation003
  Font = Sans Serif
  LineSpace = 80
  LockPosition = false
  MaxWidth = -1
  Rotation = 0
  ScaleType = 0
  Text = Drill 5/64" - Depth 6.0mm | Tap M2.5x0.45
  TextSize = 2.5
  TextStyle = 0
  X = 151.717
  Y = 30.2802
FEATURE [TechDraw::DrawViewAnnotation] Annotation004
  Font = Sans Serif
  LineSpace = 80
  LockPosition = false
  MaxWidth = -1
  Rotation = 0
  ScaleType = 0
  Text = Drill 7.20mm | Counterbore 12.0mm | Depth 2.18mm
  TextSize = 2.5
  TextStyle = 0
  X = 106.454
  Y = 149.635
FEATURE [TechDraw::DrawViewDimension] Dimension056
  Arbitrary = false
  ArbitraryTolerances = false
  EqualTolerance = false
  FormatSpec = %.2f
  FormatSpecOverTolerance = %+.2f
  FormatSpecUnderTolerance = %+.2f
  Inverted = false
  LockPosition = false
  MeasureType = 1
  OverTolerance = 0
  References2D = -> [ProjItem007]
  Rotation = 0
  ScaleType = 0
  TheoreticalExact = false
  Type = 2
  UnderTolerance = 0
  X = 28.3752
  Y = 1.21565
FEATURE [TechDraw::DrawViewAnnotation] Annotation005
  Font = Sans Serif
  LineSpace = 80
  LockPosition = false
  MaxWidth = -1
  Rotation = 0
  ScaleType = 0
  Text = Through-drill 3/32" & tap M3x0.5
  TextSize = 2.5
  TextStyle = 0
  X = 236.033
  Y = 126.03
FEATURE [TechDraw::DrawViewAnnotation] Annotation006
  Font = Sans Serif
  LineSpace = 80
  LockPosition = false
  MaxWidth = -1
  Rotation = 0
  ScaleType = 0
  Text = Drill 5/32" - Depth 10.0mm | Tap M5x0.8
  TextSize = 2.5
  TextStyle = 0
  X = 204.142
  Y = 82.1491
FEATURE [TechDraw::DrawViewDimension] Dimension057
  Arbitrary = false
  ArbitraryTolerances = false
  EqualTolerance = false
  FormatSpec = %.2f
  FormatSpecOverTolerance = %+.2f
  FormatSpecUnderTolerance = %+.2f
  Inverted = false
  LockPosition = false
  MeasureType = 1
  OverTolerance = 0
  References2D = -> [ProjItem007]
  Rotation = 0
  ScaleType = 0
  TheoreticalExact = false
  Type = 1
  UnderTolerance = 0
  X = -14.2126
  Y = 0.579442
FEATURE [TechDraw::DrawViewDimension] Dimension058
  Arbitrary = false
  ArbitraryTolerances = false
  EqualTolerance = false
  FormatSpec = %.2f
  FormatSpecOverTolerance = %+.2f
  FormatSpecUnderTolerance = %+.2f
  Inverted = false
  LockPosition = false
  MeasureType = 1
  OverTolerance = 0
  References2D = -> [ProjItem007]
  Rotation = 0
  ScaleType = 0
  TheoreticalExact = false
  Type = 2
  UnderTolerance = 0
  X = 16.8932
  Y = -8.86083
FEATURE [TechDraw::DrawViewDimension] Dimension059
  Arbitrary = false
  ArbitraryTolerances = false
  EqualTolerance = false
  FormatSpec = %.2f
  FormatSpecOverTolerance = %+.2f
  FormatSpecUnderTolerance = %+.2f
  Inverted = false
  LockPosition = false
  MeasureType = 1
  OverTolerance = 0
  References2D = -> [ProjItem009]
  Rotation = 0
  ScaleType = 0
  TheoreticalExact = false
  Type = 1
  UnderTolerance = 0
  X = 12.9638
  Y = -1.97335
FEATURE [TechDraw::DrawLeaderLine] LeaderLine
  AutoHorizontal = true
  EndSymbol = 7
  LeaderParent = -> ProjItem009
  LockPosition = true
  Rotation = 0
  Scalable = false
  ScaleType = 0
  StartSymbol = 0
  WayPoints = (3) [(0,0,0),(-224.773,-77.6001,0),(-166.796,-77.6001,0)]
  X = -1.79941
  Y = 0.349869
FEATURE [TechDraw::DrawLeaderLine] LeaderLine001
  AutoHorizontal = true
  EndSymbol = 7
  LeaderParent = -> ProjItem009
  LockPosition = true
  Rotation = 0
  Scalable = false
  ScaleType = 0
  StartSymbol = 0
  WayPoints = (3) [(0,0,0),(-68.577,183.451,0),(-97.1196,183.451,0)]
  X = -2.70674
  Y = -16.5506
FEATURE [TechDraw::DrawLeaderLine] LeaderLine002
  AutoHorizontal = true
  EndSymbol = 7
  LeaderParent = -> ProjItem009
  LockPosition = true
  Rotation = 0
  Scalable = false
  ScaleType = 0
  StartSymbol = 0
  WayPoints = (3) [(0,0,0),(80.2759,208.717,0),(72.2586,208.717,0)]
  X = 18.4429
  Y = -22.4083
FEATURE [TechDraw::DrawLeaderLine] LeaderLine003
  AutoHorizontal = true
  EndSymbol = 7
  LeaderParent = -> ProjItem007
  LockPosition = true
  Rotation = 0
  Scalable = false
  ScaleType = 0
  StartSymbol = 0
  WayPoints = (3) [(0,0,0),(130.582,-100.612,0),(28.8993,-100.612,0)]
  X = 15.0953
  Y = 21.8222
FEATURE [TechDraw::DrawLeaderLine] LeaderLine004
  AutoHorizontal = true
  EndSymbol = 7
  LeaderParent = -> ProjItem010
  LockPosition = true
  Rotation = 0
  Scalable = false
  ScaleType = 0
  StartSymbol = 0
  WayPoints = (3) [(0,0,0),(160.242,-169.036,0),(48.8544,-169.036,0)]
  X = 6.30669
  Y = -17.0626
FEATURE [TechDraw::DrawLeaderLine] LeaderLine005
  AutoHorizontal = true
  EndSymbol = 7
  LeaderParent = -> ProjItem012
  LockPosition = true
  Rotation = 0
  Scalable = false
  ScaleType = 0
  StartSymbol = 0
  WayPoints = (3) [(0,0,0),(55.2298,-68.074,0),(346.792,-68.074,0)]
  X = -5.81726
  Y = 1.79244
FEATURE [TechDraw::DrawLeaderLine] LeaderLine006
  AutoHorizontal = true
  EndSymbol = 7
  LeaderParent = -> ProjItem012
  LockPosition = true
  Rotation = 0
  Scalable = false
  ScaleType = 0
  StartSymbol = 0
  WayPoints = (3) [(0,0,0),(83.487,113.029,0),(211.928,113.029,0)]
  X = 9.21039
  Y = -5.91405
FEATURE [TechDraw::DrawViewDimension] Dimension060
  Arbitrary = false
  ArbitraryTolerances = false
  EqualTolerance = false
  FormatSpec = %.2f
  FormatSpecOverTolerance = %+.2f
  FormatSpecUnderTolerance = %+.2f
  Inverted = false
  LockPosition = false
  MeasureType = 1
  OverTolerance = 0
  References2D = -> [ProjItem013]
  Rotation = 0
  ScaleType = 0
  TheoreticalExact = false
  Type = 2
  UnderTolerance = 0
  X = -15.7965
  Y = -8.8593
FEATURE [TechDraw::DrawLeaderLine] LeaderLine007
  AutoHorizontal = true
  EndSymbol = 7
  LeaderParent = -> ProjItem012
  LockPosition = true
  Rotation = 0
  Scalable = false
  ScaleType = 0
  StartSymbol = 0
  WayPoints = (3) [(0,0,0),(-136.48,122.41,0),(-289.843,122.41,0)]
  X = -16.9452
  Y = -11.0576
FEATURE [TechDraw::DrawViewAnnotation] Annotation007
  Font = Sans Serif
  LineSpace = 80
  LockPosition = false
  MaxWidth = -1
  Rotation = 0
  ScaleType = 0
  Text = Pocket to provide clearance |  for Hemera Heatbreak | Depth 4.0mm
  TextSize = 2.5
  TextStyle = 0
  X = 45.3136
  Y = 24.4432
FEATURE [TechDraw::DrawViewDimension] Dimension061
  Arbitrary = false
  ArbitraryTolerances = false
  EqualTolerance = false
  FormatSpec = %.2f
  FormatSpecOverTolerance = %+.2f
  FormatSpecUnderTolerance = %+.2f
  Inverted = false
  LockPosition = false
  MeasureType = 1
  OverTolerance = 0
  References2D = -> [ProjItem012]
  Rotation = 0
  ScaleType = 0
  TheoreticalExact = false
  Type = 2
  UnderTolerance = 0
  X = 24.7033
  Y = 25.7597
FEATURE [TechDraw::DrawViewDimension] Dimension062
  Arbitrary = false
  ArbitraryTolerances = false
  EqualTolerance = false
  FormatSpec = %.2f
  FormatSpecOverTolerance = %+.2f
  FormatSpecUnderTolerance = %+.2f
  Inverted = false
  LockPosition = false
  MeasureType = 1
  OverTolerance = 0
  References2D = -> [ProjItem012]
  Rotation = 0
  ScaleType = 0
  TheoreticalExact = false
  Type = 2
  UnderTolerance = 0
  X = 18.2398
  Y = 26.1674
FEATURE [TechDraw::DrawViewDimension] Dimension063
  Arbitrary = false
  ArbitraryTolerances = false
  EqualTolerance = false
  FormatSpec = %.2f
  FormatSpecOverTolerance = %+.2f
  FormatSpecUnderTolerance = %+.2f
  Inverted = false
  LockPosition = false
  MeasureType = 1
  OverTolerance = 0
  References2D = -> [ProjItem012]
  Rotation = 0
  ScaleType = 0
  TheoreticalExact = false
  Type = 1
  UnderTolerance = 0
  X = -21.2141
  Y = -1.32694
FEATURE [TechDraw::DrawViewDimension] Dimension064
  Arbitrary = false
  ArbitraryTolerances = false
  EqualTolerance = false
  FormatSpec = %.2f
  FormatSpecOverTolerance = %+.2f
  FormatSpecUnderTolerance = %+.2f
  Inverted = false
  LockPosition = false
  MeasureType = 1
  OverTolerance = 0
  References2D = -> [ProjItem012]
  Rotation = 0
  ScaleType = 0
  TheoreticalExact = false
  Type = 1
  UnderTolerance = 0
  X = -8.89372
  Y = -7.61363
FEATURE [TechDraw::DrawLeaderLine] LeaderLine008
  AutoHorizontal = true
  EndSymbol = 7
  LeaderParent = -> ProjItem007
  LockPosition = true
  Rotation = 0
  Scalable = false
  ScaleType = 0
  StartSymbol = 0
  WayPoints = (3) [(0,0,0),(299.692,157.585,0),(353.158,157.585,0)]
  X = 1.42174
  Y = -17.8935
FEATURE [TechDraw::DrawViewAnnotation] Annotation008
  Font = Sans Serif
  LineSpace = 80
  LockPosition = false
  MaxWidth = -1
  Rotation = 0
  ScaleType = 0
  Text = Drill 3/32" - Depth 7.0mm | Tap M3x0.5
  TextSize = 2.5
  TextStyle = 0
  X = 156.865
  Y = 84.0309
FEATURE [TechDraw::DrawPage] Page002  label="watercooled_printhead_dwg"
  KeepUpdated = false
  NextBalloonIndex = 1
  ProjectionType = 0
  Template = -> Template002
  Views = -> [View002,ProjGroup002,Dimension024,Dimension025,Dimension026,Dimension028,Dimension029,Dimension030,Dimension031,Dimension032,Dimension033,Dimension035,Dimension036,Dimension037,Dimension038,Dimension039,Dimension040,Dimension042,Dimension043,Dimension044,Dimension045,Dimension046,Dimension047,Dimension048,Dimension049,Dimension050,Dimension051,Dimension052,Annotation,Dimension053,Dimension054,+27 more]
FEATURE [PartDesign::CoordinateSystem] LCS_1
  AttacherType = Attacher::AttachEngine3D
  MapMode = 11
  Placement = pos=(-14.17,-15,40.95) rot=(0.707107,0,0.707107;3.14159rad)
  Support = -> [Hole014]
FEATURE [PartDesign::CoordinateSystem] LCS_2
  AttacherType = Attacher::AttachEngine3D
  MapMode = 11
  Placement = pos=(-14.17,15,40.95) rot=(0.707107,0,0.707107;3.14159rad)
  Support = -> [Hole014]
FEATURE [PartDesign::CoordinateSystem] LCS_3
  AttacherType = Attacher::AttachEngine3D
  MapMode = 11
  Placement = pos=(-18.35,-16,5.5) rot=(0,-1,0;1.5708rad)
  Support = -> [Hole014]
FEATURE [PartDesign::CoordinateSystem] LCS_4
  AttacherType = Attacher::AttachEngine3D
  MapMode = 11
  Placement = pos=(6.35,12,5.5) rot=(0.57735,0.57735,0.57735;4.18879rad)
  Support = -> [Hole014]
FEATURE [PartDesign::CoordinateSystem] LCS_5
  AttacherType = Attacher::AttachEngine3D
  MapMode = 11
  Placement = pos=(-6.35,12,5.5) rot=(0.57735,0.57735,0.57735;4.18879rad)
  Support = -> [Hole014]
FEATURE [PartDesign::CoordinateSystem] LCS_6
  AttacherType = Attacher::AttachEngine3D
  MapMode = 11
  Placement = pos=(15.5,-3.95,15) rot=(0,0,1;1.5708rad)
  Support = -> [Hole014]
FEATURE [PartDesign::CoordinateSystem] LCS_7
  AttacherType = Attacher::AttachEngine3D
  MapMode = 11
  Placement = pos=(0,-6,1e-15) rot=(0.707107,0.707107,0;3.14159rad)
  Support = -> [Hole014]
FEATURE [PartDesign::CoordinateSystem] LCS_8
  AttacherType = Attacher::AttachEngine3D
  MapMode = 11
  Placement = pos=(-18.35,8e-15,9.05) rot=(0,-1,0;1.5708rad)
  Support = -> [Hole014]
FEATURE [PartDesign::CoordinateSystem] LCS_9
  AttacherType = Attacher::AttachEngine3D
  MapMode = 11
  Placement = pos=(-18.35,-15,40.95) rot=(0.707107,0,-0.707107;3.14159rad)
  Support = -> [Hole014]
FEATURE [PartDesign::CoordinateSystem] LCS_10
  AttacherType = Attacher::AttachEngine3D
  MapMode = 11
  Placement = pos=(-18.35,15,40.95) rot=(0.707107,0,-0.707107;3.14159rad)
  Support = -> [Hole014]
FEATURE [App::Part] Part  label="watercooled_block"
  Group = -> [Body021,LCS_1,LCS_2,LCS_3,LCS_4,LCS_5,LCS_6,LCS_7,LCS_8,LCS_9,LCS_10]
  Origin = -> Origin
